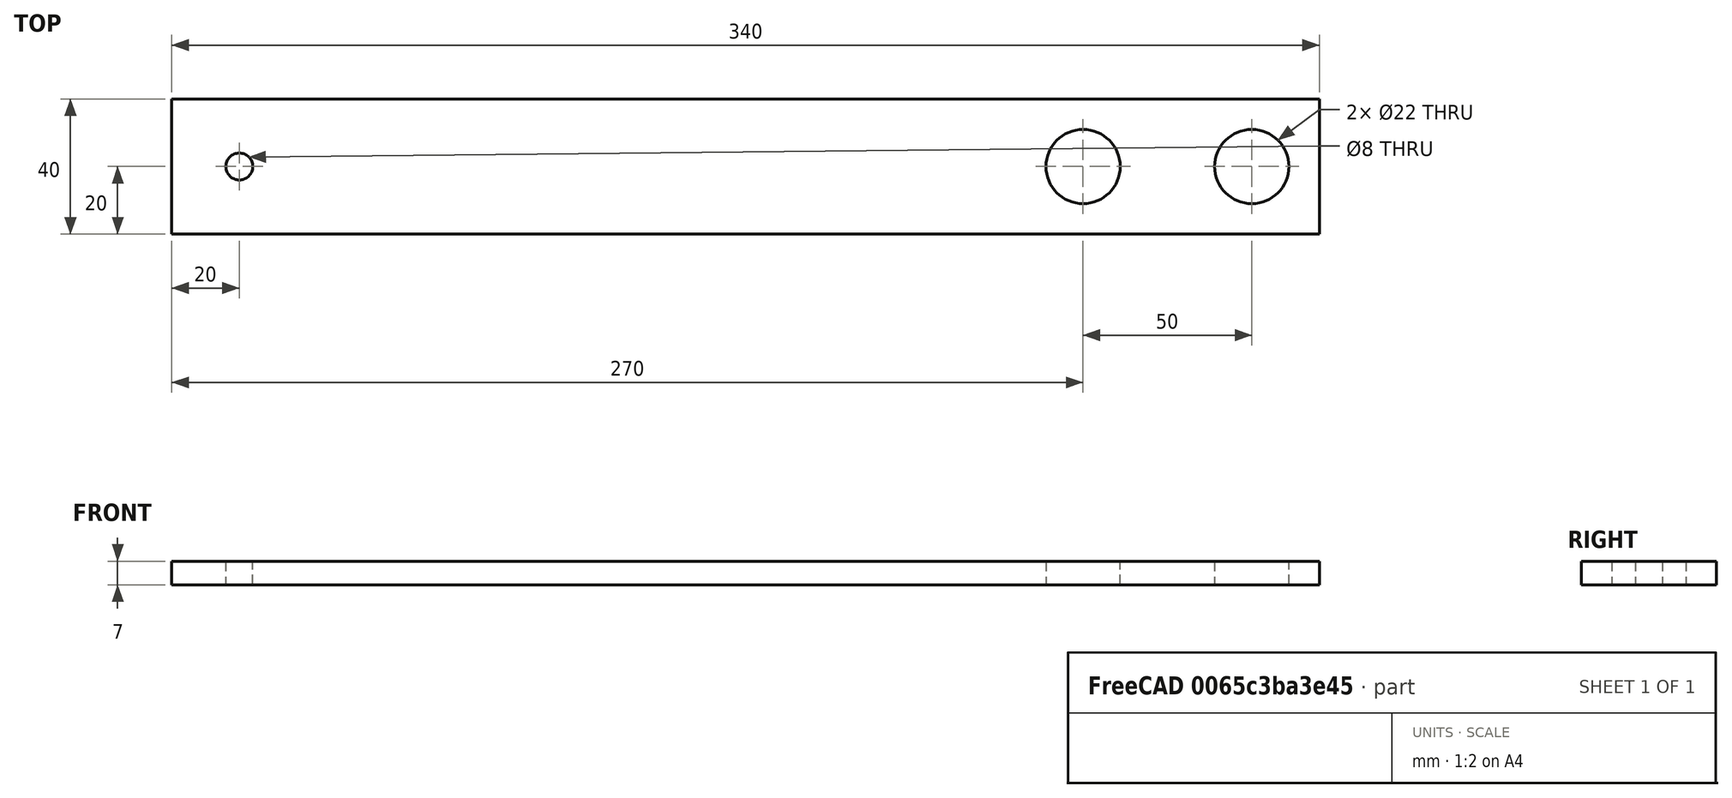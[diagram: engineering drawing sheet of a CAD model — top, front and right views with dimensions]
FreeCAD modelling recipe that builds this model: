
FCSTD DOCUMENT  (FreeCAD 0.19R24276 (Git))
Label: richag_250_edge
License: All rights reserved
LicenseURL: http://en.wikipedia.org/wiki/All_rights_reserved
objects: Sketcher::SketchObject×1, PartDesign::Pad×1, PartDesign::Body×1
note: 4 computed .brp shape members not serialized (recipe doc carries the construction recipe); baked Part::Feature solids carry a one-line shape summary decoded from their .brp

FEATURE [Sketcher::SketchObject] Sketch
  FullyConstrained = false
  MapMode = 5
  Support = -> [XY_Plane]
  sketch-geometry (7):
    g0: Circle CenterX=0 CenterY=0 CenterZ=0 NormalX=0 NormalY=0 NormalZ=1 AngleXU=0 Radius=11
    g1: Circle CenterX=50 CenterY=0 CenterZ=0 NormalX=0 NormalY=0 NormalZ=1 AngleXU=0 Radius=11
    g2: LineSegment StartX=-270 StartY=20 StartZ=0 EndX=70 EndY=20 EndZ=0
    g3: LineSegment StartX=70 StartY=20 StartZ=0 EndX=70 EndY=-20 EndZ=0
    g4: LineSegment StartX=70 StartY=-20 StartZ=0 EndX=-270 EndY=-20 EndZ=0
    g5: LineSegment StartX=-270 StartY=-20 StartZ=0 EndX=-270 EndY=20 EndZ=0
    g6: Circle CenterX=-250 CenterY=0 CenterZ=0 NormalX=0 NormalY=0 NormalZ=1 AngleXU=0 Radius=4
  constraints (10):
    c: Coincident(g0,g-1)
    c: Distance(g0,g1) = 50
    c: Distance(g6,g0) = 250
    c: DistanceX(g2,g6) = 20
    c: DistanceX(g1,g2) = 20
    c: Perpendicular(g3,g4)
    c: Perpendicular(g2,g3)
    c: Perpendicular(g5,g2)
    c: DistanceY(g3,g1) = 20
    c: DistanceY(g1,g2) = 20
FEATURE [PartDesign::Pad] Pad
  Direction = (1,1,1)
  Length = 7
  Length2 = 100
  Profile = -> Sketch
  Type = 0
FEATURE [PartDesign::Body] Body  label="Body_richag_250_edge"
  Group = -> [Sketch,Pad]
  Origin = -> Origin
  Tip = -> Pad
